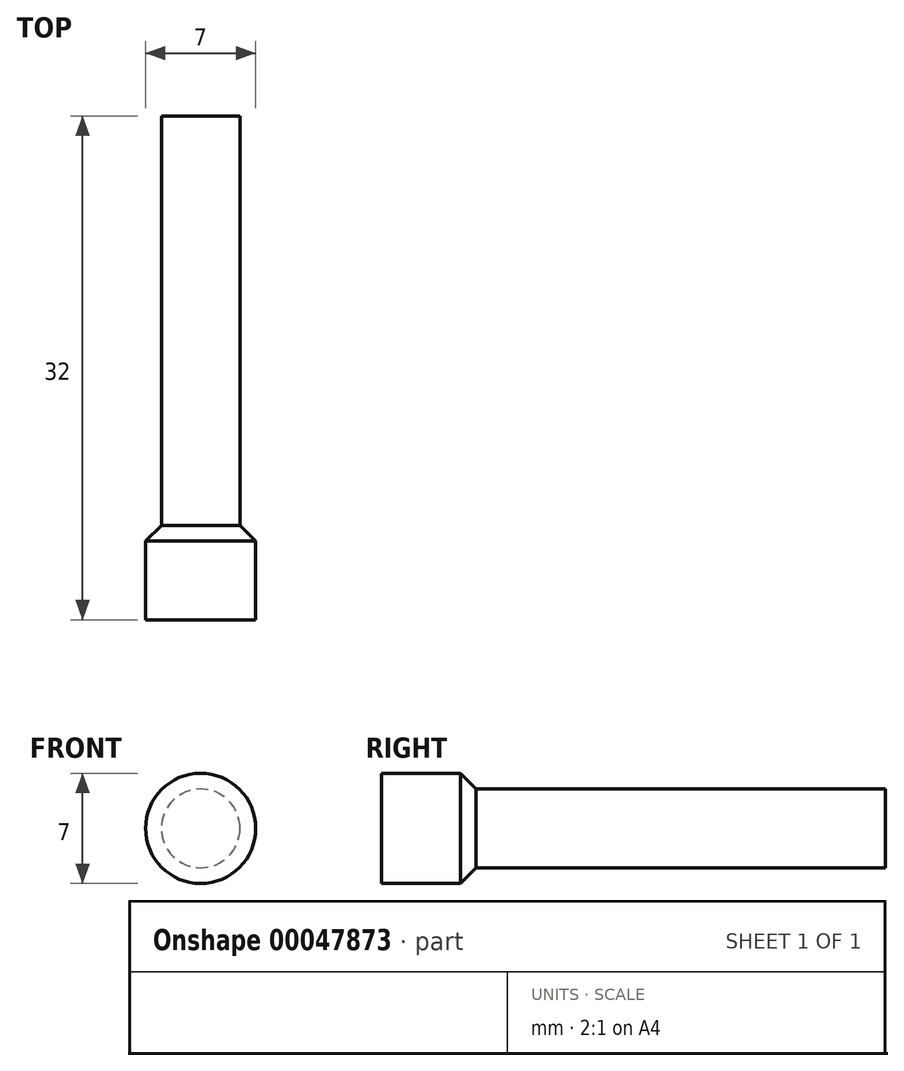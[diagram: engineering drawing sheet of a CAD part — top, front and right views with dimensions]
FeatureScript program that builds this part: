
annotation { "Feature Type Name" : "Feature", "Feature Type Description" : "" }
export const myFeature = defineFeature(function(context is Context, id is Id, definition is map)
    precondition{}
    {
        {
            var Q0;
            Q0=qCreatedBy(makeId("Front.planeOp"),FACE);
            var sketch = newSketch(context, id + "F0", { "sketchPlane" : qUnion([Q0])});
            skCircle(sketch, "E0", {"center": v(0, 0) * mm, "radius": 2.5 * mm});
            skSolve(sketch);
        }
        {
            var Q0;
            Q0=makeQuery(id+"F0.imprint","IMPRINT",FACE,{"disambiguationData":[TD([[makeQuery(id+"F0.imprint","IMPRINT",EDGE,{"derivedFrom":sQuery(id+"F0.wireOp",EDGE,"E0")}),1.0]])]});
            extrude(context, id + "F1", {"entities" : qUnion([Q0]), "depth" : 25 * mm});
        }
        {
            var Q0;
            Q0=makeQuery(id+"F1.opExtrude","CAP_FACE",FACE,{"disambiguationData":[OSD([sQuery(id+"F0.wireOp",EDGE,"E0")])],"isStart":false});
            var sketch = newSketch(context, id + "F2", { "sketchPlane" : qUnion([Q0])});
            skCircle(sketch, "E1", {"center": v(0, 0) * mm, "radius": 3.5 * mm});
            skSolve(sketch);
        }
        {
            var Q0;
            Q0=makeQuery(id+"F2.imprint","IMPRINT",FACE,{"disambiguationData":[TD([[makeQuery(id+"F2.imprint","IMPRINT",EDGE,{"derivedFrom":sQuery(id+"F2.wireOp",EDGE,"E1")}),1.0]])]});
            var Q1;
            Q1=makeQuery(id+"F2.imprint","IMPRINT",FACE,{"disambiguationData":[TD([[makeQuery(id+"F2.imprint","IMPRINT",EDGE,{"derivedFrom":makeQuery(id+"F1.opExtrude","CAP_EDGE",EDGE,{"disambiguationData":[OSD([sQuery(id+"F0.wireOp",EDGE,"E0")])],"isStart":false})}),1.0]])]});
            extrude(context, id + "F3", {"entities" : qUnion([Q0, Q1]), "operationType" : NewBodyOperationType.ADD, "depth" : 7 * mm});
        }
        {
            var Q0;
            Q0=makeQuery(id+"F3.opExtrude","CAP_EDGE",EDGE,{"disambiguationData":[OSD([sQuery(id+"F2.wireOp",EDGE,"E1")])],"isStart":true});
            chamfer(context, id + "F4", {"entities" : qUnion([Q0]), "width" : 2 * mm, "tangentPropagation" : true});
        }
    });
